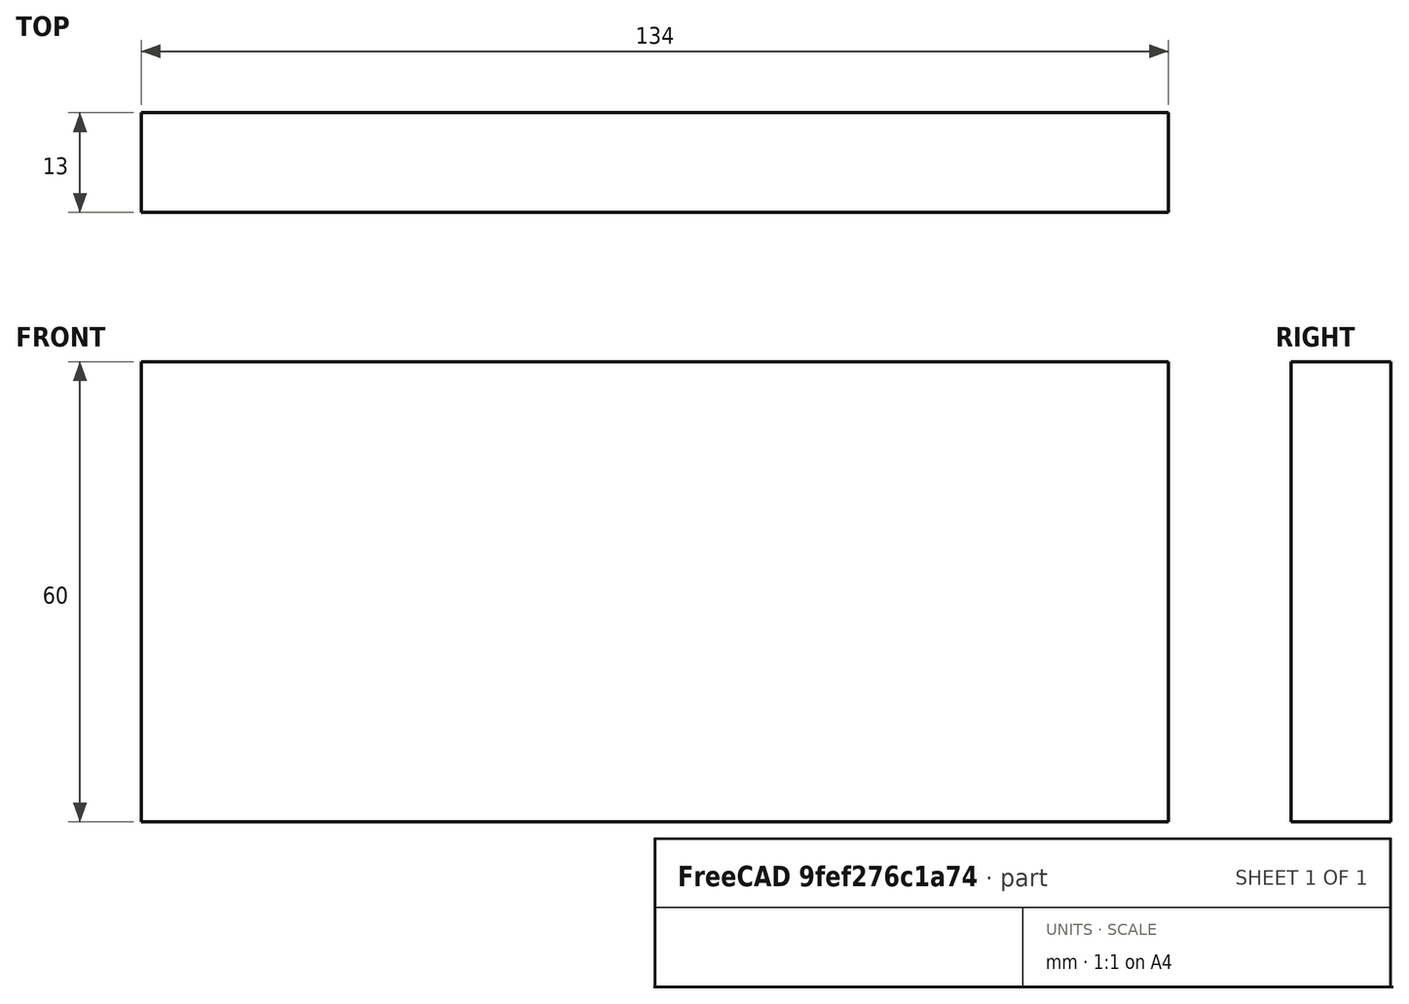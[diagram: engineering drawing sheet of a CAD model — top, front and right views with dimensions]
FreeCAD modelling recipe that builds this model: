
FCSTD DOCUMENT  (FreeCAD 0.20R29177 (Git))
Label: 1001_keyboard_sidewall_16_
License: All rights reserved
LicenseURL: http://en.wikipedia.org/wiki/All_rights_reserved
objects: Sketcher::SketchObject×1, PartDesign::Pad×1, PartDesign::Body×1, Spreadsheet::Sheet×1
note: 4 computed .brp shape members not serialized (recipe doc carries the construction recipe); baked Part::Feature solids carry a one-line shape summary decoded from their .brp

FEATURE [Sketcher::SketchObject] Sketch  label="SideWall"
  FullyConstrained = true
  MapMode = 5
  Placement = pos=(0,0,0) rot=(1,0,0;1.5708rad)
  Support = -> [XZ_Plane]
  expr: .Constraints.z_0 = <<xls>>.z_0
  expr: Constraints[10] = <<xls>>.X0
  sketch-geometry (4):
    g0: LineSegment StartX=134 StartY=0 StartZ=0 EndX=0 EndY=0 EndZ=0
    g1: LineSegment StartX=0 StartY=0 StartZ=0 EndX=0 EndY=60 EndZ=0
    g2: LineSegment StartX=0 StartY=60 StartZ=0 EndX=134 EndY=60 EndZ=0
    g3: LineSegment StartX=134 StartY=60 StartZ=0 EndX=134 EndY=0 EndZ=0
  constraints (11):
    c: Coincident(g0,g-1)
    c: Horizontal(g0)
    c: Coincident(g1,g-1)
    c: Vertical(g1)
    c: Coincident(g2,g1)
    c: Vertical(g3)
    c: Coincident(g0,g3)
    c: Perpendicular(g1,g2)
    c: DistanceY(g1,g1) = 60  'z_0'
    c: Coincident(g3,g2)
    c: DistanceX(g2,g2) = 134
FEATURE [PartDesign::Pad] Pad
  AllowMultiFace = false
  Direction = (0,-1,-1.035e-13)
  Length = 13
  Length2 = 13
  Placement = pos=(0,0,0) rot=(1,0,0;1.5708rad)
  Profile = -> Sketch
  Reversed = true
  Type = 0
FEATURE [PartDesign::Body] Body
  Group = -> [Sketch,Pad]
  Origin = -> Origin
  Tip = -> Pad
FEATURE [Spreadsheet::Sheet] Spreadsheet  label="xls"
  cells = C2=INHERITED DIMENSIONS; C3=Thickness; D3=kbf_t_0; E3=16; F3=mm; H3=NOTE: No plexi; C5=SIDEWALL ; C6=thickness of board; D6=t; E6(nt)=14; F6=mm; C7=Depth of Board; E7=150; G7=NOMINAL; C8=Depth of board; D8=X0; E8(X0)==+E7 - E3; F8=mm; G8=REAL; C9=Height of board; D9=Z0; E9(z_0)=60; F9=mm
